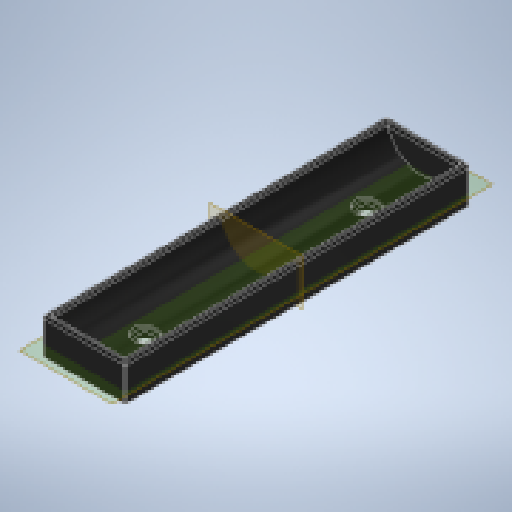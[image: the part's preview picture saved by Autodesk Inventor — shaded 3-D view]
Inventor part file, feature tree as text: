
AUTODESK INVENTOR PART (.ipt)
format: ipt  version: 2025.1 (Build 291241020, 241B)  size: 504,320 bytes
history: native  units: mm
features: sketch x3, extrude x2, plane x2, mirror x1, fillet x1, hole x1
ambient origin geometry x8: Origin, YZ Plane, XZ Plane, XY Plane, X Axis, Y Axis, Z Axis, Center Point
bodies: Body1 (feature_tree)
feature tree (10):
  extrude  "Extrusion3"  Depth=20.0mm
  plane  "Work Plane1"
  extrude  "Extrusion4"  Depth=3.0mm
  mirror  "Mirror1"
  fillet  "Fillet1"  Radius=3.0mm
  plane  "Work Plane2"
  hole  "Hole1"  [1 undecoded]
  sketch  "Sketch3"  dims[d6=16.5mm d9=20.0mm]
  sketch  "Sketch4"  dims[d10=150.0mm d11=0.0mm d12=38.0mm d13=3.0mm]
  sketch  "Sketch5"  dims[d14=3.0mm d16=1.0mm d17=3.0mm d18=0.0mm d19=-5.0mm d20=19.0mm d21=100.0mm d22=28.0mm d23=28.0mm d24=6.0mm d25=6.0mm d26=10.0mm d27=2.5mm d28=90.0deg d29=8.0mm d30=20.594885mm]
note: 1 required parameter value undecoded (feature->parameter linkage not recoverable at this tier; creation-order binding heuristic only, values carry confidence <= 0.55)
